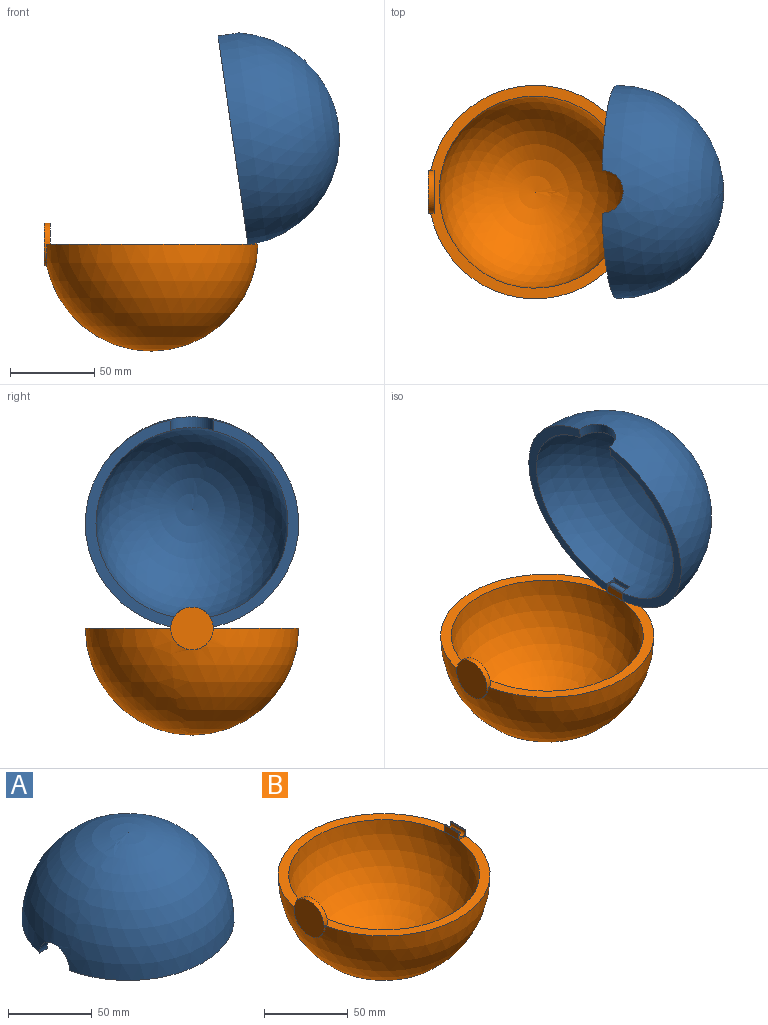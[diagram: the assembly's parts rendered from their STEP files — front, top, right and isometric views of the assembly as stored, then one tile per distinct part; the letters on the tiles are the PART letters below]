
ASSEMBLY  parts=2 mates=1
PART A: 9 faces, bbox 127x127x63.5 mm
  f0: sphere r=57.15mm, area 20184mm2, adj f2,f3,f4,f6,f7,f8
  f1: sphere r=63.5mm, area 24998.5mm2, adj f2,f3,f4,f6,f7,f8
  f2: plane 125.4x57.15mm, normal (0,0,-1), area 1081.8mm2, adj f0,f1,f6,f8
  f3: plane 125.4x57.15mm, normal (0,0,-1), area 1081.8mm2, adj f0,f1,f7,f8
  f4: plane 12.7x6.74mm, normal (0,0,-1), area 81.2mm2, adj f0,f1,f6,f7
  f5: cylinder r=2.22mm len=12.7mm, axis (0,-1,0), area 176.9mm2, adj f6,f7
  f6: plane 6.76x6.37mm, normal (0,-1,0), area 25.2mm2, adj f0,f1,f2,f4,f5
  f7: plane 6.76x6.37mm, normal (0,1,0), area 25.2mm2, adj f0,f1,f3,f4,f5
  f8: cylinder r=12.7mm len=25.4mm, axis (-1,0,0), area 259.2mm2, adj f0,f1,f2,f3
PART B: 17 faces, bbox 127x127x76.2 mm
  f0: sphere r=63.5mm, area 25079.4mm2, adj f1,f14
  f1: plane 127x125.72mm, normal (0,0,1), area 2267.8mm2, adj f0,f2,f3,f11,f12,f13,f14,f15
  f2: sphere r=57.15mm, area 20521.7mm2, adj f1
  f3: plane 12.19x4.47mm, normal (1,0,-0.07), area 54.7mm2, adj f1,f4,f12,f13
  f4: cylinder r=0.25mm len=12.19mm, axis (0,1,0), area 5.7mm2, adj f3,f5,f12,f13
  f5: plane 12.19x0.12mm, normal (-0.2,0,0.98), area 1.5mm2, adj f4,f6,f12,f13
  f6: cylinder r=0.25mm len=12.19mm, axis (0,1,0), area 5.9mm2, adj f5,f7,f12,f13
  f7: cylinder r=2.29mm len=12.19mm, axis (0,1,0), area 119.1mm2, adj f6,f8,f12,f13
  f8: cylinder r=0.25mm len=12.19mm, axis (0,1,0), area 5.9mm2, adj f7,f9,f12,f13
  f9: plane 12.19x0.82mm, normal (0.27,0,0.96), area 10.4mm2, adj f8,f10,f12,f13
  f10: cylinder r=0.25mm len=12.19mm, axis (0,1,0), area 5.7mm2, adj f9,f11,f12,f13
  f11: plane 12.19x4.84mm, normal (-1,0,0), area 59mm2, adj f1,f10,f12,f13
  f12: plane 5.74x5.09mm, normal (0,-1,0), area 11.9mm2, adj f1,f3,f4,f5,f6,f7,f8,f9
  f13: plane 5.74x5.09mm, normal (0,1,0), area 11.9mm2, adj f1,f3,f4,f5,f6,f7,f8,f9
  f14: cylinder r=12.7mm len=25.4mm, axis (-1,0,0), area 182.9mm2, adj f0,f1,f15,f16
  f15: plane 25.4x12.7mm, normal (1,0,0), area 253.4mm2, adj f1,f14
  f16: plane 25.4x25.4mm, normal (-1,0,0), area 506.7mm2, adj f14
PLACE A rot(axis=(0,1,0),81.8deg) t=(112.11,0,62.44)mm
PLACE B t=(63.5,0,0)mm
MATE revolute B.f7 <-> A.f5  axis (0,1,0) through (123.82,0,3.18)mm
